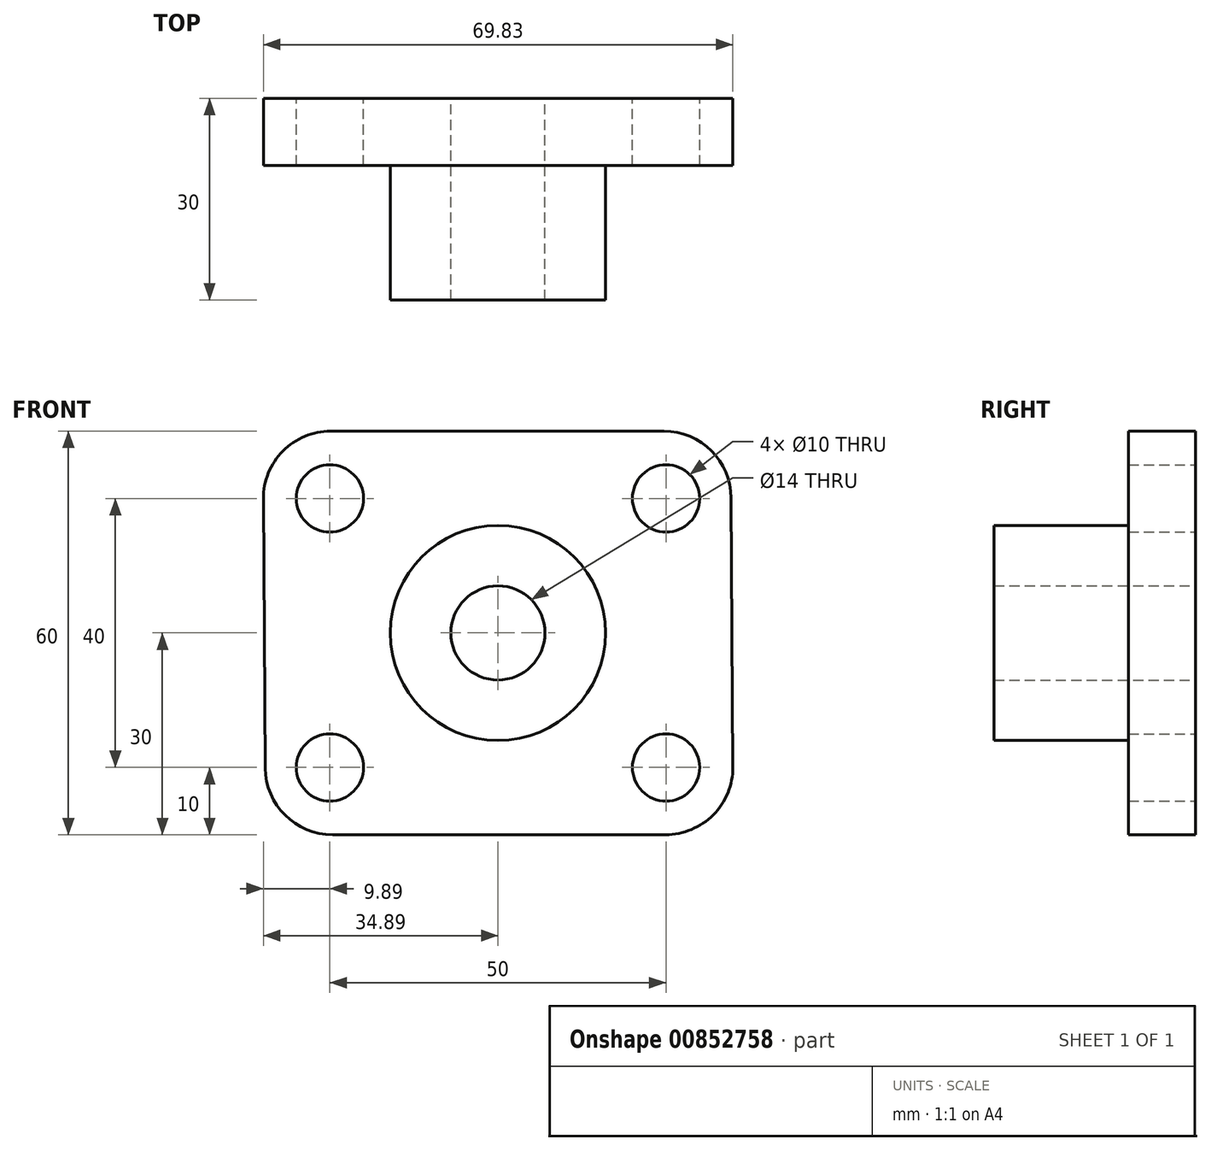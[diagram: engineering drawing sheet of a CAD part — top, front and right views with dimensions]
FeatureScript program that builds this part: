
annotation { "Feature Type Name" : "Feature", "Feature Type Description" : "" }
export const myFeature = defineFeature(function(context is Context, id is Id, definition is map)
    precondition{}
    {
        {
            var Q0;
            Q0=qCreatedBy(makeId("Front.planeOp"),FACE);
            var sketch = newSketch(context, id + "F0", { "sketchPlane" : qUnion([Q0])});
            skCircle(sketch, "E0", {"center": v(0, 0) * mm, "radius": 16 * mm});
            skLineSegment(sketch, "E1", {"start": v(0, 0) * mm, "end": v(-30, 0) * mm});
            skLineSegment(sketch, "E2", {"start": v(0, 0) * mm, "end": v(30, 0) * mm});
            skLineSegment(sketch, "E3", {"start": v(0, 0) * mm, "end": v(0, 30) * mm});
            skLineSegment(sketch, "E4", {"start": v(0, 0) * mm, "end": v(0, -30) * mm});
            skLineSegment(sketch, "E5", {"start": v(30, 0) * mm, "end": v(25, 0) * mm});
            skLineSegment(sketch, "E6", {"start": v(25, 0) * mm, "end": v(25, -20) * mm});
            skLineSegment(sketch, "E7", {"start": v(25, 0) * mm, "end": v(25, 20) * mm});
            skCircle(sketch, "E8", {"center": v(25, 20) * mm, "radius": 5 * mm});
            skCircle(sketch, "E9", {"center": v(25, -20) * mm, "radius": 5 * mm});
            skLineSegment(sketch, "E10", {"start": v(-30, 0) * mm, "end": v(-25, 0) * mm});
            skLineSegment(sketch, "E11", {"start": v(-25, 0) * mm, "end": v(-25, 20) * mm});
            skLineSegment(sketch, "E12", {"start": v(-25, 0) * mm, "end": v(-25, -20) * mm});
            skCircle(sketch, "E13", {"center": v(-25, -20) * mm, "radius": 5 * mm});
            skCircle(sketch, "E14", {"center": v(-25, 20) * mm, "radius": 5 * mm});
            skLineSegment(sketch, "E15", {"start": v(30, 20) * mm, "end": v(35, 20) * mm});
            skLineSegment(sketch, "E16", {"start": v(30, -20.29) * mm, "end": v(35, -20.29) * mm});
            skLineSegment(sketch, "E17", {"start": v(-30, -20.18) * mm, "end": v(-35, -20.18) * mm});
            skLineSegment(sketch, "E18", {"start": v(-29.96, 20.61) * mm, "end": v(-34.96, 20.61) * mm});
            skLineSegment(sketch, "E19", {"start": v(0, 30) * mm, "end": v(34.62, 30) * mm});
            skLineSegment(sketch, "E20", {"start": v(34.62, 30) * mm, "end": v(35, -29.99) * mm});
            skLineSegment(sketch, "E21", {"start": v(35, -29.99) * mm, "end": v(-34.54, -30) * mm});
            skLineSegment(sketch, "E22", {"start": v(-34.54, -30) * mm, "end": v(-34.96, 30) * mm});
            skLineSegment(sketch, "E23", {"start": v(-34.96, 30) * mm, "end": v(0, 30) * mm});
            skSolve(sketch);
        }
        {
            var Q0;
            {var subQ5=sQuery(id+"F0.wireOp",EDGE,"E23");Q0=makeQuery(id+"F0.imprint","IMPRINT",FACE,{"disambiguationData":[TD([[makeQuery(id+"F0.imprint","IMPRINT",EDGE,{"derivedFrom":subQ5}),-1.0]])]});}
            var Q1;
            {var subQ9=sQuery(id+"F0.wireOp",EDGE,"E19");Q1=makeQuery(id+"F0.imprint","IMPRINT",FACE,{"disambiguationData":[TD([[makeQuery(id+"F0.imprint","IMPRINT",EDGE,{"derivedFrom":subQ9}),-1.0]])]});}
            var Q2;
            {var subQ3=sQuery(id+"F0.wireOp",EDGE,"E0");var subQ6=sQuery(id+"F0.wireOp",EDGE,"E2");var subQ10=makeQuery(id+"F0.imprint","INTERSECT",VERTEX,{"derivedFrom":[subQ3,subQ6]});Q2=makeQuery(id+"F0.imprint","IMPRINT",FACE,{"disambiguationData":[TD([[makeQuery(id+"F0.imprint","IMPRINT",EDGE,{"disambiguationData":[TD([[subQ10,1.0]])],"derivedFrom":subQ3}),-1.0]])]});}
            var Q3;
            {var subQ1=sQuery(id+"F0.wireOp",EDGE,"E1");var subQ8=sQuery(id+"F0.wireOp",EDGE,"E0");var subQ12=makeQuery(id+"F0.imprint","INTERSECT",VERTEX,{"derivedFrom":[subQ8,subQ1]});Q3=makeQuery(id+"F0.imprint","IMPRINT",FACE,{"disambiguationData":[TD([[makeQuery(id+"F0.imprint","IMPRINT",EDGE,{"disambiguationData":[TD([[subQ12,-1.0]])],"derivedFrom":subQ8}),-1.0]])]});}
            var Q4;
            {var subQ5=sQuery(id+"F0.wireOp",EDGE,"E17");var subQ6=sQuery(id+"F0.wireOp",EDGE,"E13");var subQ7=makeQuery(id+"F0.imprint","INTERSECT",VERTEX,{"derivedFrom":[subQ6,subQ5]});Q4=makeQuery(id+"F0.imprint","IMPRINT",FACE,{"disambiguationData":[TD([[makeQuery(id+"F0.imprint","IMPRINT",EDGE,{"disambiguationData":[TD([[subQ7,1.0]])],"derivedFrom":subQ6}),-1.0]])]});}
            var Q5;
            {var subQ0=sQuery(id+"F0.wireOp",EDGE,"E15");var subQ1=sQuery(id+"F0.wireOp",EDGE,"E8");var subQ2=makeQuery(id+"F0.imprint","INTERSECT",VERTEX,{"derivedFrom":[subQ1,subQ0]});Q5=makeQuery(id+"F0.imprint","IMPRINT",FACE,{"disambiguationData":[TD([[makeQuery(id+"F0.imprint","IMPRINT",EDGE,{"disambiguationData":[TD([[subQ2,1.0]])],"derivedFrom":subQ1}),-1.0]])]});}
            var Q6;
            {var subQ0=sQuery(id+"F0.wireOp",EDGE,"E1");var subQ1=sQuery(id+"F0.wireOp",EDGE,"E0");var subQ2=makeQuery(id+"F0.imprint","INTERSECT",VERTEX,{"derivedFrom":[subQ1,subQ0]});Q6=makeQuery(id+"F0.imprint","IMPRINT",FACE,{"disambiguationData":[TD([[makeQuery(id+"F0.imprint","IMPRINT",EDGE,{"disambiguationData":[TD([[subQ2,-1.0]])],"derivedFrom":subQ1}),1.0]])]});}
            var Q7;
            {var subQ0=sQuery(id+"F0.wireOp",EDGE,"E3");var subQ1=sQuery(id+"F0.wireOp",EDGE,"E0");var subQ2=makeQuery(id+"F0.imprint","INTERSECT",VERTEX,{"derivedFrom":[subQ1,subQ0]});Q7=makeQuery(id+"F0.imprint","IMPRINT",FACE,{"disambiguationData":[TD([[makeQuery(id+"F0.imprint","IMPRINT",EDGE,{"disambiguationData":[TD([[subQ2,-1.0]])],"derivedFrom":subQ1}),1.0]])]});}
            var Q8;
            {var subQ0=sQuery(id+"F0.wireOp",EDGE,"E3");var subQ1=sQuery(id+"F0.wireOp",EDGE,"E0");var subQ2=makeQuery(id+"F0.imprint","INTERSECT",VERTEX,{"derivedFrom":[subQ1,subQ0]});Q8=makeQuery(id+"F0.imprint","IMPRINT",FACE,{"disambiguationData":[TD([[makeQuery(id+"F0.imprint","IMPRINT",EDGE,{"disambiguationData":[TD([[subQ2,1.0]])],"derivedFrom":subQ1}),1.0]])]});}
            var Q9;
            {var subQ0=sQuery(id+"F0.wireOp",EDGE,"E2");var subQ1=sQuery(id+"F0.wireOp",EDGE,"E0");var subQ2=makeQuery(id+"F0.imprint","INTERSECT",VERTEX,{"derivedFrom":[subQ1,subQ0]});Q9=makeQuery(id+"F0.imprint","IMPRINT",FACE,{"disambiguationData":[TD([[makeQuery(id+"F0.imprint","IMPRINT",EDGE,{"disambiguationData":[TD([[subQ2,1.0]])],"derivedFrom":subQ1}),1.0]])]});}
            extrude(context, id + "F1", {"entities" : qUnion([Q0, Q1, Q2, Q3, Q4, Q5, Q6, Q7, Q8, Q9]), "depth" : 10 * mm, "offsetDistance" : 25 * mm});
        }
        {
            var Q0;
            Q0=makeQuery(id+"F1.opExtrude","SWEPT_EDGE",EDGE,{"disambiguationData":[OSD([sQuery(id+"F0.wireOp",EDGE,"E19"),sQuery(id+"F0.wireOp",EDGE,"E20")])]});
            var Q1;
            Q1=makeQuery(id+"F1.opExtrude","SWEPT_EDGE",EDGE,{"disambiguationData":[OSD([sQuery(id+"F0.wireOp",EDGE,"E22"),sQuery(id+"F0.wireOp",EDGE,"E23")])]});
            var Q2;
            Q2=makeQuery(id+"F1.opExtrude","SWEPT_EDGE",EDGE,{"disambiguationData":[OSD([sQuery(id+"F0.wireOp",EDGE,"E20"),sQuery(id+"F0.wireOp",EDGE,"E21")])]});
            var Q3;
            Q3=makeQuery(id+"F1.opExtrude","SWEPT_EDGE",EDGE,{"disambiguationData":[OSD([sQuery(id+"F0.wireOp",EDGE,"E21"),sQuery(id+"F0.wireOp",EDGE,"E22")])]});
            fillet(context, id + "F2", {"entities" : qUnion([Q0, Q1, Q2, Q3]), "radius" : 10 * mm, "tangentPropagation" : true, "allowEdgeOverflow" : false});
        }
        {
            var Q0;
            Q0=makeQuery(id+"F1.opExtrude","CAP_FACE",FACE,{"disambiguationData":[OSD([sQuery(id+"F0.wireOp",EDGE,"E8"),sQuery(id+"F0.wireOp",EDGE,"E9"),sQuery(id+"F0.wireOp",EDGE,"E13"),sQuery(id+"F0.wireOp",EDGE,"E14"),sQuery(id+"F0.wireOp",EDGE,"E19"),sQuery(id+"F0.wireOp",EDGE,"E20"),sQuery(id+"F0.wireOp",EDGE,"E21"),sQuery(id+"F0.wireOp",EDGE,"E22"),sQuery(id+"F0.wireOp",EDGE,"E23")])],"isStart":false});
            var sketch = newSketch(context, id + "F3", { "sketchPlane" : qUnion([Q0])});
            skCircle(sketch, "E24", {"center": v(0, 0) * mm, "radius": 16 * mm});
            skSolve(sketch);
        }
        {
            var Q0;
            Q0=makeQuery(id+"F3.imprint","IMPRINT",FACE,{"disambiguationData":[TD([[makeQuery(id+"F3.imprint","IMPRINT",EDGE,{"derivedFrom":sQuery(id+"F3.wireOp",EDGE,"E24")}),1.0]])]});
            extrude(context, id + "F4", {"entities" : qUnion([Q0]), "operationType" : NewBodyOperationType.ADD, "depth" : 20 * mm, "offsetDistance" : 25 * mm});
        }
        {
            var Q0;
            Q0=sQuery(id+"F0.wireOp",VERTEX,"E1.start");
            var Q1;
            Q1=makeQuery(id+"F1.opExtrude","SWEPT_BODY",BODY,{"disambiguationData":[OSD([sQuery(id+"F0.wireOp",EDGE,"E8"),sQuery(id+"F0.wireOp",EDGE,"E9"),sQuery(id+"F0.wireOp",EDGE,"E13"),sQuery(id+"F0.wireOp",EDGE,"E14"),sQuery(id+"F0.wireOp",EDGE,"E19"),sQuery(id+"F0.wireOp",EDGE,"E20"),sQuery(id+"F0.wireOp",EDGE,"E21"),sQuery(id+"F0.wireOp",EDGE,"E22"),sQuery(id+"F0.wireOp",EDGE,"E23")])]});
            hole(context, id + "F5", {"style" : HoleStyle.SIMPLE, "endStyle" : HoleEndStyle.BLIND, "oppositeDirection" : true, "standardTappedOrClearance" : lookupTablePath({ "standard" : "ISO", "engagement" : "75%", "pitch" : "2 mm", "size" : "M16", "type" : "Tapped" }), "standardBlindInLast" : lookupTablePath({ "standard" : "ISO", "engagement" : "75%", "pitch" : "2 mm", "size" : "M16", "type" : "Tapped" }), "holeDiameter" : 14 * mm, "majorDiameter" : 16 * mm, "showTappedDepth" : true, "holeDepth" : 31 * mm, "isTappedThrough" : true, "tappedDepth" : 25 * mm, "tapClearance" : 3, "locations" : qUnion([Q0]), "scope" : qUnion([Q1])});
        }
    });
